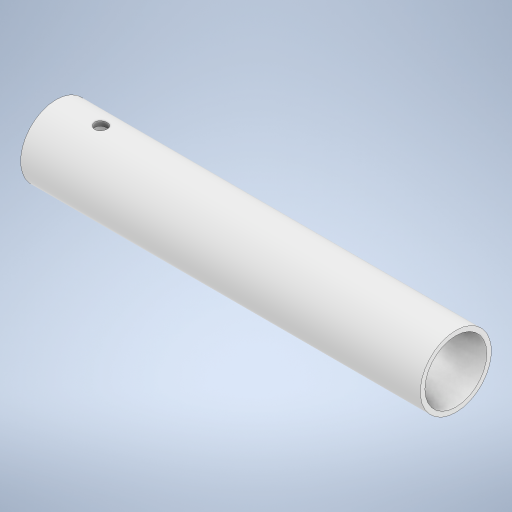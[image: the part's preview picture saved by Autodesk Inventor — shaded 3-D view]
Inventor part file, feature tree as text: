
AUTODESK INVENTOR PART (.ipt)
format: ipt  version: 2023 (Build 270158030, 158C)  size: 245,248 bytes
history: native  units: in
note: dims shown in document units (in); Inventor stores cm internally (conversion verified against a paired STEP export)
features: extrude x2, sketch x2
ambient origin geometry x8: Origin, YZ Plane, XZ Plane, XY Plane, X Axis, Y Axis, Z Axis, Center Point
bodies: Solid1 (feature_tree)
feature tree (4):
  extrude  "Extrusion1"  Depth=0.154in
  extrude  "Extrusion2"  Depth=0.4134in
  sketch  "Sketch1"  dims[d0=2.067in d1=0.154in]
  sketch  "Sketch2"  dims[d2=13.3465in d3=0.0in d4=0.4134in d5=1.5in d6=0.0in d7=0.0in]
